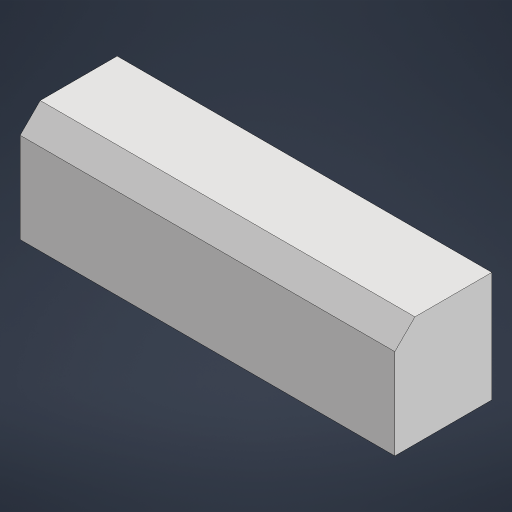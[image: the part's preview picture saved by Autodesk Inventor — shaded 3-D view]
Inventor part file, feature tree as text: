
AUTODESK INVENTOR PART (.ipt)
format: ipt  version: 2023.1 (Build 271208000, 208)  size: 143,872 bytes
history: native  units: in
note: dims shown in document units (in); Inventor stores cm internally (conversion verified against a paired STEP export)
features: extrude x1, sketch x1
ambient origin geometry x8: Origin, YZ Plane, XZ Plane, XY Plane, X Axis, Y Axis, Z Axis, Center Point
bodies: Solid1 (feature_tree)
feature tree (2):
  extrude  "Extrusion1"  Depth=4.125in
  sketch  "Sketch2"  dims[d3=3.625in d4=4.125in d5=2.875in d6=3.375in d7=14.0in d8=0.0in]
